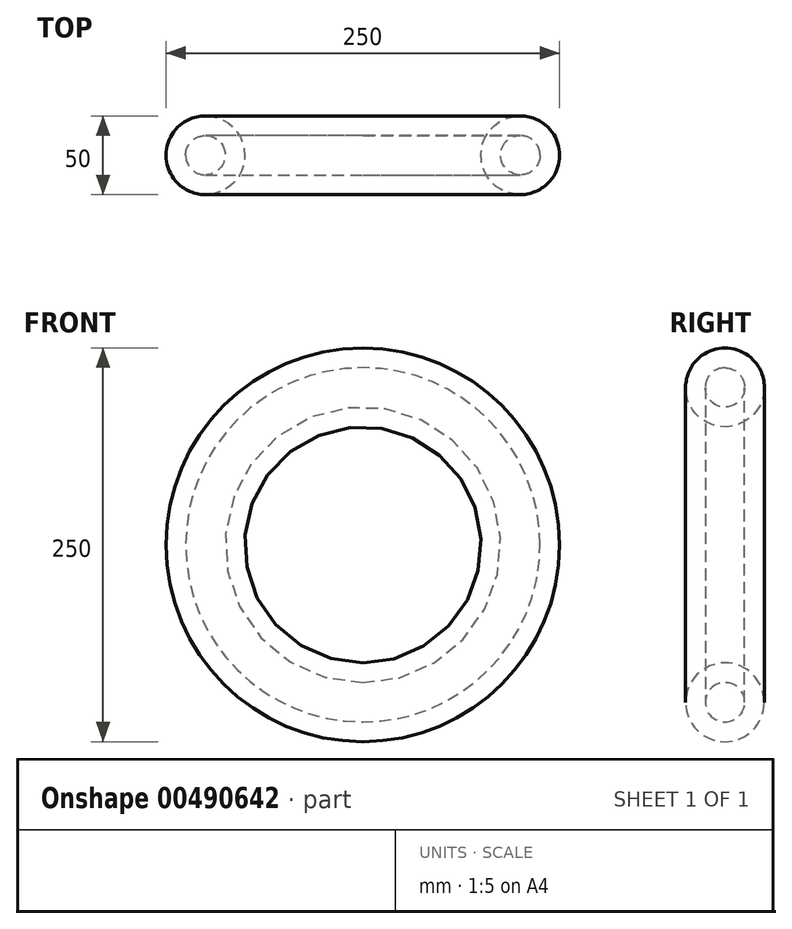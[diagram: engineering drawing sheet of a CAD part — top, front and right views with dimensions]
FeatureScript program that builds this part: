
annotation { "Feature Type Name" : "Feature", "Feature Type Description" : "" }
export const myFeature = defineFeature(function(context is Context, id is Id, definition is map)
    precondition{}
    {
        {
            var Q0;
            Q0=qCreatedBy(makeId("Top.planeOp"),FACE);
            var sketch = newSketch(context, id + "F0", { "sketchPlane" : qUnion([Q0])});
            skCircle(sketch, "E0", {"center": v(0, 0) * mm, "radius": 25 * mm});
            skCircle(sketch, "E1", {"center": v(0, 0) * mm, "radius": 12.5 * mm});
            skSolve(sketch);
        }
        {
            var Q0;
            Q0=qCreatedBy(makeId("Front.planeOp"),FACE);
            var sketch = newSketch(context, id + "F1", { "sketchPlane" : qUnion([Q0])});
            skCircle(sketch, "E2", {"center": v(-100, 0) * mm, "radius": 100 * mm});
            skSolve(sketch);
        }
        {
            var Q0;
            Q0=makeQuery(id+"F0.imprint","IMPRINT",FACE,{"disambiguationData":[TD([[makeQuery(id+"F0.imprint","IMPRINT",EDGE,{"derivedFrom":sQuery(id+"F0.wireOp",EDGE,"E0")}),1.0]])]});
            var Q1;
            Q1=sQuery(id+"F1.wireOp",EDGE,"E2");
            sweep(context, id + "F2", {"profiles" : qUnion([Q0]), "path" : qUnion([Q1])});
        }
    });
